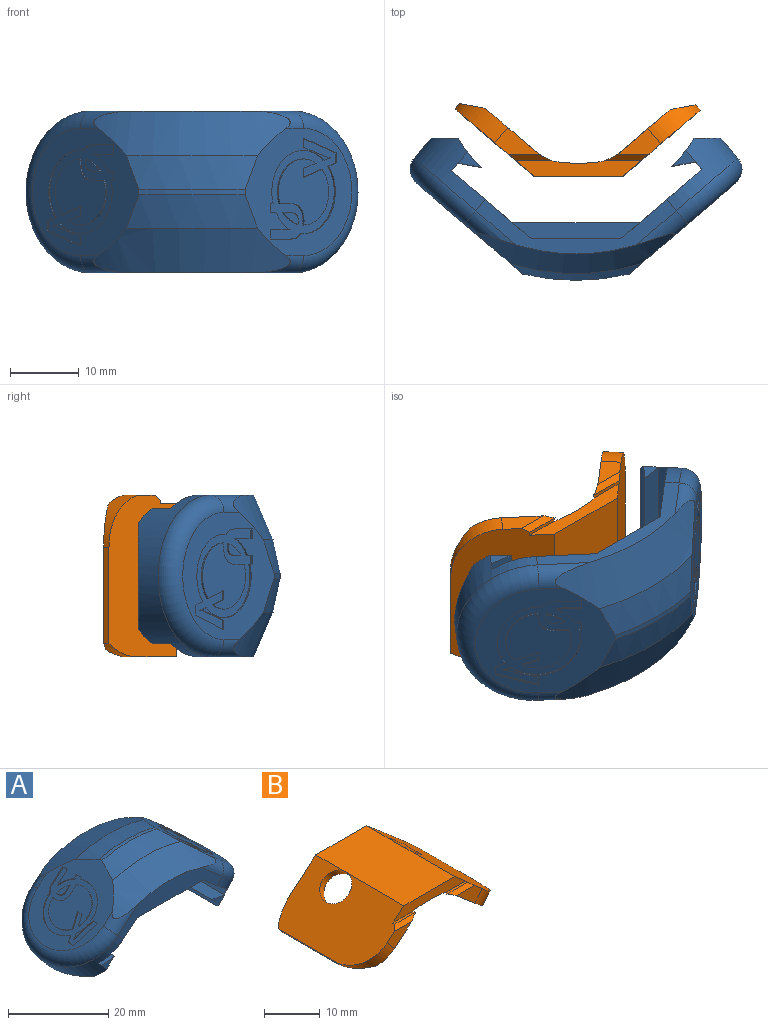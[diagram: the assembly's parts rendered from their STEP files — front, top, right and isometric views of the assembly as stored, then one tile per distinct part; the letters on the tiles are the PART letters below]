
ASSEMBLY  parts=2 mates=1
PART A: 220 faces, bbox 50.7x26.5x24.2 mm
  f0: plane 19.05x16.08mm, normal (0.65,0,0.76), area 158.9mm2, adj f27,f34,f35,f36,f37,f38,f39,f40
  f1: plane 19.05x16.08mm, normal (-0.65,0,0.76), area 158.9mm2, adj f27,f34,f35,f36,f37,f41,f42,f43
  f2: plane 20.57x16.8mm, normal (0.65,0,-0.76), area 311.5mm2, adj f10,f12,f46,f47,f108,f109,f110,f111
  f3: plane 20.57x17.09mm, normal (-0.65,0,-0.76), area 297.6mm2, adj f15,f44,f48,f49,f54,f55,f56,f57
  f4: plane 19.74x3.47mm, normal (-0.18,0,0.98), area 69.7mm2, adj f5,f21,f52,f53
  f5: cylinder r=20.13mm len=19.74mm, axis (0,-1,0), area 103.7mm2, adj f4,f6,f29,f52,f53
  f6: cylinder r=11.81mm len=23.62mm, axis (-0.65,0,0.76), area 146.7mm2, adj f5,f19,f21,f22,f29,f30,f31,f42
  f7: plane 19.38x3.49mm, normal (0.18,0,0.98), area 68.9mm2, adj f8,f23,f50,f51
  f8: cylinder r=20.13mm len=19.38mm, axis (0,-1,0), area 97.8mm2, adj f7,f9,f28,f50,f51
  f9: cylinder r=11.81mm len=23.62mm, axis (0.65,0,0.76), area 144.3mm2, adj f8,f23,f24,f25,f28,f30,f31,f39
  f10: cylinder r=1.52mm len=2.01mm, axis (-0.65,0,0.76), area 2mm2, adj f2,f11,f46,f47
  f11: torus R=12.7mm, axis (0,1,0), area 96.1mm2, adj f10,f44,f45,f46,f47,f48
  f12: cylinder r=10.29mm len=20.57mm, axis (0.65,0,-0.76), area 176.6mm2, adj f2,f19,f20,f21,f46,f47,f219
  f13: bspline ~11.23x4.8mm, area 4.8mm2, adj f18,f22,f47
  f14: bspline ~15.91x9.98mm, area 4.8mm2, adj f18,f19,f46
  f15: cylinder r=10.29mm len=20.57mm, axis (-0.65,0,-0.76), area 153.8mm2, adj f3,f23,f26,f48,f49,f215,f217
  f16: bspline ~5.86x4.5mm, area 8.5mm2, adj f18,f48,f215,f216
  f17: bspline ~15.92x9.99mm, area 8.5mm2, adj f18,f49,f217,f218
  f18: plane 23.12x13.75mm, normal (0,0,-1), area 226.4mm2, adj f13,f14,f16,f17,f19,f22,f24,f25
  f19: plane 13.42x11.6mm, normal (0.65,0,-0.76), area 33.8mm2, adj f6,f12,f14,f18,f21,f30,f32,f33
  f20: plane 15.97x2.89mm, normal (-0.65,0,0.76), area 42.2mm2, adj f12,f21
  f21: plane 19.8x1.94mm, normal (0.76,0,0.65), area 25.1mm2, adj f4,f6,f12,f19,f20,f22,f219
  f22: plane 13.42x11.61mm, normal (0.65,0,-0.76), area 16.6mm2, adj f6,f13,f18,f21,f31,f47,f219
  f23: plane 19.38x1.88mm, normal (-0.76,0,0.65), area 25.6mm2, adj f7,f9,f15,f24,f25,f26,f215,f217
  f24: plane 11.85x10.12mm, normal (-0.65,0,-0.76), area 10.9mm2, adj f9,f18,f23,f30,f32,f33,f215
  f25: plane 11.85x10.12mm, normal (-0.65,0,-0.76), area 15.1mm2, adj f9,f18,f23,f31,f217
  f26: plane 15.51x2.68mm, normal (0.65,0,0.76), area 38mm2, adj f15,f23
  f27: cylinder r=33.02mm len=15.5mm, axis (0,-1,0), area 11.9mm2, adj f0,f1,f36,f37
  f28: plane 15.7x3.93mm, normal (0,0,-1), area 42.3mm2, adj f8,f9
  f29: plane 15.7x3.93mm, normal (0,0,-1), area 42.3mm2, adj f5,f6
  f30: plane 29.25x7.95mm, normal (0,-1,0), area 102.8mm2, adj f6,f9,f19,f24,f32,f34,f40,f41
  f31: plane 29.25x7.95mm, normal (0,1,0), area 64.4mm2, adj f6,f9,f18,f22,f25,f35,f38,f43
  f32: plane 18.72x1.14mm, normal (0,0,-1), area 21.4mm2, adj f19,f24,f30,f33
  f33: plane 18.72x2.42mm, normal (0,1,0), area 38.4mm2, adj f18,f19,f24,f32
  f34: cone r=29.21mm half-angle=23.2deg, axis (0,1,0), area 181.7mm2, adj f0,f1,f30,f36,f40,f41
  f35: cone r=33.02mm half-angle=23.2deg, axis (0,-1,0), area 181.7mm2, adj f0,f1,f31,f37,f38,f43
  f36: cone r=33.02mm half-angle=11.6deg, axis (0,1,0), area 87.2mm2, adj f0,f1,f27,f34
  f37: cone r=33.02mm half-angle=11.6deg, axis (0,-1,0), area 87.2mm2, adj f0,f1,f27,f35
  f38: cylinder r=2.54mm len=7.47mm, axis (-0.76,0,0.65), area 16.1mm2, adj f0,f31,f35,f39
  f39: torus R=9.27mm, axis (0.65,0,0.76), area 136.5mm2, adj f0,f9,f38,f40
  f40: cylinder r=2.54mm len=7.47mm, axis (-0.76,0,0.65), area 16.1mm2, adj f0,f30,f34,f39
  f41: cylinder r=2.54mm len=7.47mm, axis (-0.76,0,-0.65), area 16.1mm2, adj f1,f30,f34,f42
  f42: torus R=9.27mm, axis (-0.65,0,0.76), area 136.5mm2, adj f1,f6,f41,f43
  f43: cylinder r=2.54mm len=7.47mm, axis (-0.76,0,-0.65), area 16.1mm2, adj f1,f31,f35,f42
  f44: cylinder r=1.91mm len=5.15mm, axis (0.65,0,0.76), area 11.8mm2, adj f3,f11,f18,f48,f49
  f45: cylinder r=1.52mm len=2.44mm, axis (-0.65,0,0.76), area 6mm2, adj f11,f18,f46,f47
  f46: cylinder r=12.7mm len=5.61mm, axis (0.65,0,-0.76), area 15mm2, adj f2,f10,f11,f12,f14,f18,f19,f45
  f47: cylinder r=12.7mm len=6.97mm, axis (-0.65,0,0.76), area 17.7mm2, adj f2,f10,f11,f12,f13,f18,f22,f45
  f48: cylinder r=12.7mm len=6mm, axis (0.65,0,0.76), area 16.9mm2, adj f3,f11,f15,f16,f18,f44,f216
  f49: cylinder r=12.7mm len=6mm, axis (-0.65,0,-0.76), area 17.1mm2, adj f3,f15,f17,f18,f44,f218
  f50: plane 3.49x2.32mm, normal (0,1,0), area 3.3mm2, adj f7,f8,f9
  f51: plane 3.49x2.32mm, normal (0,-1,0), area 3.3mm2, adj f7,f8,f9
  f52: plane 3.47x2.27mm, normal (0,1,0), area 3.1mm2, adj f4,f5,f6
  f53: plane 3.47x2.27mm, normal (0,-1,0), area 3.1mm2, adj f4,f5,f6
  f54: plane 1.1x0.99mm, normal (0,1,0), area 0.3mm2, adj f3,f55,f61,f62
  f55: plane 0.8x0.19mm, normal (0.76,0,-0.65), area 0.2mm2, adj f3,f54,f56,f62
  f56: plane 2.77x2.42mm, normal (0,-1,0), area 0.9mm2, adj f3,f55,f57,f62
  f57: plane 0.8x0.19mm, normal (-0.76,0,0.65), area 0.2mm2, adj f3,f56,f58,f62
  f58: plane 1.1x0.99mm, normal (0,1,0), area 0.3mm2, adj f3,f57,f59,f62
  f59: plane 3.73x0.19mm, normal (-0.76,0,0.65), area 0.9mm2, adj f3,f58,f60,f62
  f60: plane 0.9x0.82mm, normal (0,1,0), area 0.2mm2, adj f3,f59,f61,f62
  f61: plane 3.73x0.19mm, normal (0.76,0,-0.65), area 0.9mm2, adj f3,f54,f60,f62
  f62: plane 4.53x2.6mm, normal (-0.65,0,-0.76), area 6.3mm2, adj f54,f55,f56,f57,f58,f59,f60,f61
  f63: plane 2.93x0.19mm, normal (0.76,0,-0.65), area 0.7mm2, adj f3,f64,f77,f78
  f64: plane 0.89x0.82mm, normal (0,-1,0), area 0.2mm2, adj f3,f63,f65,f78
  f65: plane 2.77x0.19mm, normal (-0.76,0,0.65), area 0.7mm2, adj f3,f64,f66,f78
  f66: extruded ~0.77x0.33mm, area 0.2mm2, adj f3,f65,f67,f78
  f67: extruded ~0.68x0.64mm, area 0.2mm2, adj f3,f66,f68,f78
  f68: extruded ~0.7x0.65mm, area 0.2mm2, adj f3,f67,f69,f78
  f69: extruded ~0.77x0.33mm, area 0.2mm2, adj f3,f68,f70,f78
  f70: plane 2.78x0.19mm, normal (0.76,0,-0.65), area 0.7mm2, adj f3,f69,f71,f78
  f71: plane 0.89x0.82mm, normal (0,-1,0), area 0.2mm2, adj f3,f70,f72,f78
  f72: plane 2.92x0.19mm, normal (-0.76,0,0.65), area 0.7mm2, adj f3,f71,f73,f78
  f73: extruded ~1.23x0.53mm, area 0.3mm2, adj f3,f72,f74,f78
  f74: extruded ~1.2x1.08mm, area 0.4mm2, adj f3,f73,f75,f78
  f75: extruded ~0.93x0.85mm, area 0.3mm2, adj f3,f74,f76,f78
  f76: extruded ~0.66x0.62mm, area 0.2mm2, adj f3,f75,f77,f78
  f77: extruded ~0.88x0.34mm, area 0.2mm2, adj f3,f63,f76,f78
  f78: plane 4.6x2.83mm, normal (-0.65,0,-0.76), area 9.4mm2, adj f63,f64,f65,f66,f67,f68,f69,f70
  f79: plane 1.69x1.49mm, normal (0,1,0), area 0.5mm2, adj f3,f80,f90,f91
  f80: plane 1.99x0.19mm, normal (-0.76,0,0.65), area 0.5mm2, adj f3,f79,f81,f91
  f81: plane 1.03x0.93mm, normal (0,1,0), area 0.3mm2, adj f3,f80,f82,f91
  f82: plane 1.99x0.19mm, normal (0.76,0,-0.65), area 0.5mm2, adj f3,f81,f83,f91
  f83: plane 1.69x1.49mm, normal (0,1,0), area 0.5mm2, adj f3,f82,f84,f91
  f84: plane 1.13x0.19mm, normal (0.76,0,-0.65), area 0.3mm2, adj f3,f83,f85,f91
  f85: plane 1.69x1.49mm, normal (0,-1,0), area 0.5mm2, adj f3,f84,f86,f91
  f86: plane 2.02x0.19mm, normal (0.76,0,-0.65), area 0.5mm2, adj f3,f85,f87,f91
  f87: plane 1.03x0.93mm, normal (0,-1,0), area 0.3mm2, adj f3,f86,f88,f91
  f88: plane 2.02x0.19mm, normal (-0.76,0,0.65), area 0.5mm2, adj f3,f87,f89,f91
  f89: plane 1.69x1.49mm, normal (0,-1,0), area 0.5mm2, adj f3,f88,f90,f91
  f90: plane 1.13x0.19mm, normal (-0.76,0,0.65), area 0.3mm2, adj f3,f79,f89,f91
  f91: plane 5.14x3.9mm, normal (-0.65,0,-0.76), area 10.3mm2, adj f79,f80,f81,f82,f83,f84,f85,f86
  f92: extruded ~1.14x0.38mm, area 0.3mm2, adj f93,f105,f106,f107
  f93: extruded ~1.15x0.39mm, area 0.3mm2, adj f92,f94,f106,f107
  f94: extruded ~0.82x0.76mm, area 0.3mm2, adj f93,f95,f106,f107
  f95: extruded ~1.53x1.03mm, area 0.6mm2, adj f94,f96,f106,f107
  f96: extruded ~1.53x1.04mm, area 0.6mm2, adj f95,f105,f106,f107
  f97: extruded ~1.73x0.59mm, area 0.5mm2, adj f3,f98,f104,f106
  f98: extruded ~1.73x0.59mm, area 0.5mm2, adj f3,f97,f99,f106
  f99: extruded ~1.38x1.23mm, area 0.4mm2, adj f3,f98,f100,f106
  f100: extruded ~1.38x1.24mm, area 0.4mm2, adj f3,f99,f101,f106
  f101: extruded ~1.73x0.59mm, area 0.5mm2, adj f3,f100,f102,f106
  f102: extruded ~1.74x0.59mm, area 0.5mm2, adj f3,f101,f103,f106
  f103: extruded ~1.38x1.23mm, area 0.4mm2, adj f3,f102,f104,f106
  f104: extruded ~1.38x1.23mm, area 0.4mm2, adj f3,f97,f103,f106
  f105: extruded ~0.82x0.75mm, area 0.2mm2, adj f92,f96,f106,f107
  f106: plane 4.67x3.28mm, normal (-0.65,0,-0.76), area 10.8mm2, adj f92,f93,f94,f95,f96,f97,f98,f99
  f107: plane 3.06x1.75mm, normal (-0.65,0,-0.76), area 5.9mm2, adj f92,f93,f94,f95,f96,f105
  f108: plane 1.09x0.99mm, normal (0,1,0), area 0.3mm2, adj f2,f109,f121,f122
  f109: plane 4.53x0.19mm, normal (0.76,0,0.65), area 1.2mm2, adj f2,f108,f110,f122
  f110: plane 0.82x0.76mm, normal (0,-1,0), area 0.2mm2, adj f2,f109,f111,f122
  f111: plane 2.15x0.19mm, normal (-0.76,0,-0.65), area 0.5mm2, adj f2,f110,f112,f122
  f112: extruded ~1.25x0.22mm, area 0.3mm2, adj f2,f111,f113,f122
  f113: plane 0.21x0.18mm, normal (0,-1,0), area 0mm2, adj f2,f112,f114,f122
  f114: plane 3.4x1.66mm, normal (0.66,-0.5,0.56), area 1mm2, adj f2,f113,f115,f122
  f115: plane 1.09x0.98mm, normal (0,-1,0), area 0.3mm2, adj f2,f114,f116,f122
  f116: plane 4.53x0.19mm, normal (-0.76,0,-0.65), area 1.2mm2, adj f2,f115,f117,f122
  f117: plane 0.82x0.75mm, normal (0,1,0), area 0.2mm2, adj f2,f116,f118,f122
  f118: plane 2.13x0.19mm, normal (0.76,0,0.65), area 0.5mm2, adj f2,f117,f119,f122
  f119: extruded ~1.3x0.23mm, area 0.3mm2, adj f2,f118,f120,f122
  f120: plane 0.21x0.19mm, normal (0,1,0), area 0mm2, adj f2,f119,f121,f122
  f121: plane 3.43x1.66mm, normal (-0.66,0.5,-0.56), area 1mm2, adj f2,f108,f120,f122
  f122: plane 4.53x3.06mm, normal (0.65,0,-0.76), area 11.6mm2, adj f108,f109,f110,f111,f112,f113,f114,f115
  f123: plane 4.53x0.19mm, normal (-0.76,0,-0.65), area 1.2mm2, adj f2,f124,f126,f127
  f124: plane 0.9x0.82mm, normal (0,1,0), area 0.2mm2, adj f2,f123,f125,f127
  f125: plane 4.53x0.19mm, normal (0.76,0,0.65), area 1.2mm2, adj f2,f124,f126,f127
  f126: plane 0.9x0.82mm, normal (0,-1,0), area 0.2mm2, adj f2,f123,f125,f127
  f127: plane 4.53x0.73mm, normal (0.65,0,-0.76), area 4.4mm2, adj f123,f124,f125,f126
  f128: plane 1.69x1.49mm, normal (0,1,0), area 0.5mm2, adj f2,f129,f139,f140
  f129: plane 1.99x0.19mm, normal (-0.76,0,-0.65), area 0.5mm2, adj f2,f128,f130,f140
  f130: plane 1.03x0.93mm, normal (0,1,0), area 0.3mm2, adj f2,f129,f131,f140
  f131: plane 1.99x0.19mm, normal (0.76,0,0.65), area 0.5mm2, adj f2,f130,f132,f140
  f132: plane 1.69x1.49mm, normal (0,1,0), area 0.5mm2, adj f2,f131,f133,f140
  f133: plane 1.13x0.19mm, normal (0.76,0,0.65), area 0.3mm2, adj f2,f132,f134,f140
  f134: plane 1.69x1.49mm, normal (0,-1,0), area 0.5mm2, adj f2,f133,f135,f140
  f135: plane 2.02x0.19mm, normal (0.76,0,0.65), area 0.5mm2, adj f2,f134,f136,f140
  f136: plane 1.03x0.93mm, normal (0,-1,0), area 0.3mm2, adj f2,f135,f137,f140
  f137: plane 2.02x0.19mm, normal (-0.76,0,-0.65), area 0.5mm2, adj f2,f136,f138,f140
  f138: plane 1.69x1.49mm, normal (0,-1,0), area 0.5mm2, adj f2,f137,f139,f140
  f139: plane 1.13x0.19mm, normal (-0.76,0,-0.65), area 0.3mm2, adj f2,f128,f138,f140
  f140: plane 5.14x3.9mm, normal (0.65,0,-0.76), area 10.3mm2, adj f128,f129,f130,f131,f132,f133,f134,f135
  f141: plane 1.91x1.69mm, normal (0,1,0), area 0.6mm2, adj f142,f174,f175,f177
  f142: cylinder r=4.83mm len=6.51mm, axis (-0.65,0,0.76), area 3mm2, adj f141,f143,f175,f177
  f143: plane 1.95x1.72mm, normal (-0.23,0.95,-0.2), area 0.6mm2, adj f142,f144,f175,f177
  f144: plane 1.35x0.19mm, normal (-0.76,0,-0.65), area 0.3mm2, adj f143,f145,f175,f177
  f145: plane 2.81x2.46mm, normal (0.24,-0.95,0.21), area 0.9mm2, adj f144,f146,f175,f177
  f146: cylinder r=4.83mm len=8.11mm, axis (-0.65,0,0.76), area 2.8mm2, adj f145,f147,f175,f177
  f147: extruded ~0.53x0.21mm, area 0.1mm2, adj f146,f148,f175,f177
  f148: extruded ~1.4x0.38mm, area 0.4mm2, adj f147,f149,f175,f177
  f149: extruded ~0.9x0.78mm, area 0.3mm2, adj f148,f174,f175,f177
  f150: cylinder r=4.83mm len=2.21mm, axis (-0.65,0,0.76), area 0.8mm2, adj f151,f172,f175,f176
  f151: plane 1.16x1.05mm, normal (0,-1,0), area 0.3mm2, adj f150,f152,f175,f176
  f152: extruded ~0.98x0.89mm, area 0.3mm2, adj f151,f153,f175,f176
  f153: extruded ~0.95x0.43mm, area 0.3mm2, adj f152,f172,f175,f176
  f154: plane 0.5x0.48mm, normal (0,1,0), area 0.1mm2, adj f1,f155,f173,f175
  f155: plane 1.33x0.19mm, normal (-0.76,0,-0.65), area 0.3mm2, adj f1,f154,f156,f175
  f156: plane 0.93x0.84mm, normal (0,-1,0), area 0.3mm2, adj f1,f155,f157,f175
  f157: cylinder r=6.1mm len=2.51mm, axis (-0.65,0,0.76), area 1mm2, adj f1,f156,f158,f175
  f158: plane 3x2.61mm, normal (0,1,0), area 0.9mm2, adj f1,f157,f159,f175
  f159: plane 1.33x0.19mm, normal (-0.76,0,-0.65), area 0.3mm2, adj f1,f158,f160,f175
  f160: plane 3.25x2.83mm, normal (0,-1,0), area 1mm2, adj f1,f159,f161,f175
  f161: extruded ~1.46x1.3mm, area 0.5mm2, adj f1,f160,f162,f175
  f162: extruded ~0.25x0.23mm, area 0mm2, adj f1,f161,f163,f175
  f163: cylinder r=6.1mm len=9.82mm, axis (-0.65,0,0.76), area 3.6mm2, adj f1,f162,f164,f175
  f164: plane 1.32x1.18mm, normal (0.24,-0.95,0.21), area 0.4mm2, adj f1,f163,f165,f175
  f165: plane 1.46x0.19mm, normal (0.76,0,0.65), area 0.4mm2, adj f1,f164,f166,f175
  f166: plane 4.95x4.28mm, normal (0.24,0.95,0.21), area 1.7mm2, adj f1,f165,f167,f175
  f167: plane 1.35x0.19mm, normal (-0.76,0,-0.65), area 0.3mm2, adj f1,f166,f168,f175
  f168: plane 3.01x2.63mm, normal (-0.23,-0.95,-0.2), area 1mm2, adj f1,f167,f169,f175
  f169: extruded ~1.22x1.09mm, area 0.4mm2, adj f1,f168,f170,f175
  f170: extruded ~0.63x0.59mm, area 0.2mm2, adj f1,f169,f171,f175
  f171: extruded ~0.66x0.62mm, area 0.2mm2, adj f1,f170,f173,f175
  f172: extruded ~0.44x0.22mm, area 0.1mm2, adj f150,f153,f175,f176
  f173: cylinder r=6.1mm len=7.78mm, axis (-0.65,0,0.76), area 3.9mm2, adj f1,f154,f171,f175
  f174: extruded ~1.1x0.99mm, area 0.3mm2, adj f141,f149,f175,f177
  f175: plane 14.69x9.61mm, normal (-0.65,0,0.76), area 71.5mm2, adj f141,f142,f143,f144,f145,f146,f147,f148
  f176: plane 2.08x1.77mm, normal (-0.65,0,0.76), area 2.6mm2, adj f150,f151,f152,f153,f172
  f177: plane 9.65x7.34mm, normal (-0.65,0,0.76), area 59.8mm2, adj f141,f142,f143,f144,f145,f146,f147,f148
  f178: cylinder r=4.83mm len=2.21mm, axis (0.65,0,0.76), area 0.8mm2, adj f179,f211,f212,f214
  f179: plane 1.16x1.05mm, normal (0,1,0), area 0.3mm2, adj f178,f180,f212,f214
  f180: extruded ~0.98x0.89mm, area 0.3mm2, adj f179,f181,f212,f214
  f181: extruded ~0.95x0.43mm, area 0.3mm2, adj f180,f211,f212,f214
  f182: plane 2.81x2.46mm, normal (-0.24,0.95,0.21), area 0.9mm2, adj f183,f209,f212,f213
  f183: cylinder r=4.83mm len=8.11mm, axis (0.65,0,0.76), area 2.8mm2, adj f182,f184,f212,f213
  f184: extruded ~0.53x0.21mm, area 0.1mm2, adj f183,f185,f212,f213
  f185: extruded ~1.4x0.38mm, area 0.4mm2, adj f184,f186,f212,f213
  f186: extruded ~0.9x0.78mm, area 0.3mm2, adj f185,f187,f212,f213
  f187: extruded ~1.1x0.99mm, area 0.3mm2, adj f186,f188,f212,f213
  f188: plane 1.91x1.69mm, normal (0,-1,0), area 0.6mm2, adj f187,f189,f212,f213
  f189: cylinder r=4.83mm len=6.51mm, axis (0.65,0,0.76), area 3mm2, adj f188,f190,f212,f213
  f190: plane 1.95x1.72mm, normal (0.23,-0.95,-0.2), area 0.6mm2, adj f189,f209,f212,f213
  f191: extruded ~0.66x0.62mm, area 0.2mm2, adj f0,f192,f210,f212
  f192: cylinder r=6.1mm len=7.78mm, axis (0.65,0,0.76), area 3.9mm2, adj f0,f191,f193,f212
  f193: plane 0.5x0.48mm, normal (0,-1,0), area 0.1mm2, adj f0,f192,f194,f212
  f194: plane 1.33x0.19mm, normal (0.76,0,-0.65), area 0.3mm2, adj f0,f193,f195,f212
  f195: plane 0.93x0.84mm, normal (0,1,0), area 0.3mm2, adj f0,f194,f196,f212
  f196: cylinder r=6.1mm len=2.51mm, axis (0.65,0,0.76), area 1mm2, adj f0,f195,f197,f212
  f197: plane 3x2.61mm, normal (0,-1,0), area 0.9mm2, adj f0,f196,f198,f212
  f198: plane 1.33x0.19mm, normal (0.76,0,-0.65), area 0.3mm2, adj f0,f197,f199,f212
  f199: plane 3.25x2.83mm, normal (0,1,0), area 1mm2, adj f0,f198,f200,f212
  f200: extruded ~1.46x1.3mm, area 0.5mm2, adj f0,f199,f201,f212
  f201: extruded ~0.25x0.23mm, area 0mm2, adj f0,f200,f202,f212
  f202: cylinder r=6.1mm len=9.82mm, axis (0.65,0,0.76), area 3.6mm2, adj f0,f201,f203,f212
  f203: plane 1.32x1.18mm, normal (-0.24,0.95,0.21), area 0.4mm2, adj f0,f202,f204,f212
  f204: plane 1.46x0.19mm, normal (-0.76,0,0.65), area 0.4mm2, adj f0,f203,f205,f212
  f205: plane 4.95x4.28mm, normal (-0.24,-0.95,0.21), area 1.7mm2, adj f0,f204,f206,f212
  f206: plane 1.35x0.19mm, normal (0.76,0,-0.65), area 0.3mm2, adj f0,f205,f207,f212
  f207: plane 3.01x2.63mm, normal (0.23,0.95,-0.2), area 1mm2, adj f0,f206,f208,f212
  f208: extruded ~1.22x1.09mm, area 0.4mm2, adj f0,f207,f210,f212
  f209: plane 1.35x0.19mm, normal (0.76,0,-0.65), area 0.3mm2, adj f182,f190,f212,f213
  f210: extruded ~0.63x0.59mm, area 0.2mm2, adj f0,f191,f208,f212
  f211: extruded ~0.44x0.22mm, area 0.1mm2, adj f178,f181,f212,f214
  f212: plane 14.69x9.61mm, normal (0.65,0,0.76), area 71.5mm2, adj f178,f179,f180,f181,f182,f183,f184,f185
  f213: plane 9.65x7.34mm, normal (0.65,0,0.76), area 59.8mm2, adj f182,f183,f184,f185,f186,f187,f188,f189
  f214: plane 2.08x1.77mm, normal (0.65,0,0.76), area 2.6mm2, adj f178,f179,f180,f181,f211
  f215: cone r=10.29mm half-angle=51.3deg, axis (-0.65,0,-0.76), area 28.6mm2, adj f15,f16,f18,f23,f24,f216
  f216: cone r=11.43mm half-angle=51.3deg, axis (0.65,0,0.76), area 0mm2, adj f16,f48,f215
  f217: cone r=10.29mm half-angle=51.3deg, axis (-0.65,0,-0.76), area 28.6mm2, adj f15,f17,f18,f23,f25,f218
  f218: cone r=11.43mm half-angle=51.3deg, axis (0.65,0,0.76), area 0mm2, adj f17,f49,f217
  f219: cone r=10.29mm half-angle=51.3deg, axis (0.65,0,-0.76), area 28.7mm2, adj f12,f21,f22,f47
PART B: 62 faces, bbox 35.9x28.6x12.3 mm
  f0: plane 6.48x3.83mm, normal (0,-1,0), area 12.2mm2, adj f8,f13,f15,f47,f52
  f1: plane 6.68x4mm, normal (0,-1,0), area 13mm2, adj f7,f12,f14,f46,f51
  f2: cone r=20.13mm half-angle=9.1deg, axis (0,1,0), area 10.4mm2, adj f12,f13,f17,f50
  f3: plane 22.49x12.99mm, normal (0,0,1), area 287.2mm2, adj f7,f8,f9,f10,f11,f50
  f4: cylinder r=11.81mm len=5.98mm, axis (-0.65,0,0.76), area 11.7mm2, adj f8,f9,f28,f29,f60,f61
  f5: cylinder r=11.81mm len=6.19mm, axis (0.65,0,0.76), area 12.3mm2, adj f7,f9,f26,f27,f53,f54
  f6: cylinder r=20.13mm len=19.79mm, axis (0,-1,0), area 12.4mm2, adj f14,f26,f46,f53
  f7: plane 23.62x11.56mm, normal (0.65,0,0.76), area 304.1mm2, adj f1,f3,f5,f9,f10,f27,f46,f48
  f8: plane 23.62x11.35mm, normal (-0.65,0,0.76), area 298.2mm2, adj f0,f3,f4,f9,f11,f28,f47,f49
  f9: plane 26.12x7.12mm, normal (0,1,0), area 44.2mm2, adj f3,f4,f5,f7,f8,f55,f56,f57
  f10: cylinder r=3.26mm len=6.53mm, axis (-0.65,0,-0.76), area 35.6mm2, adj f3,f7,f40,f41,f42,f43,f44,f45
  f11: cylinder r=3.26mm len=6.53mm, axis (0.65,0,-0.76), area 35.6mm2, adj f3,f8,f34,f35,f36,f37,f38,f39
  f12: bspline ~9.89x4.98mm, area 6.3mm2, adj f1,f2,f14,f17,f19,f30,f48,f50
  f13: bspline ~12.9x5.76mm, area 6.3mm2, adj f0,f2,f15,f17,f21,f32,f49,f50
  f14: plane 21.08x7.64mm, normal (-0.65,0,-0.76), area 128.4mm2, adj f1,f6,f12,f19,f23,f30,f43,f46
  f15: plane 21.08x7.64mm, normal (0.65,0,-0.76), area 128.2mm2, adj f0,f13,f16,f21,f25,f32,f37,f47
  f16: cylinder r=20.13mm len=19.64mm, axis (0,-1,0), area 7.4mm2, adj f15,f29,f47,f61
  f17: cylinder r=23.18mm len=18.03mm, axis (0,-1,0), area 103.8mm2, adj f2,f12,f13,f18,f19,f20,f21,f22
  f18: bspline ~3.55x3.04mm, area 1.6mm2, adj f17,f19,f40
  f19: cylinder r=5.08mm len=10.28mm, axis (0,-1,0), area 25.3mm2, adj f12,f14,f17,f18,f30,f41
  f20: bspline ~3.55x3.04mm, area 1.6mm2, adj f17,f21,f38
  f21: cylinder r=5.08mm len=10.28mm, axis (0,-1,0), area 25.3mm2, adj f13,f15,f17,f20,f32,f39
  f22: bspline ~3.55x3.04mm, area 1.6mm2, adj f17,f23,f44
  f23: cylinder r=5.08mm len=2.7mm, axis (0,-1,0), area 5.6mm2, adj f14,f17,f22,f45,f56
  f24: bspline ~3.55x3.04mm, area 1.6mm2, adj f17,f25,f34
  f25: cylinder r=5.08mm len=2.7mm, axis (0,-1,0), area 5.6mm2, adj f15,f17,f24,f35,f58
  f26: plane 21.35x3.87mm, normal (-0.18,0,-0.98), area 71.4mm2, adj f5,f6,f27,f46,f53
  f27: plane 14.07x0.77mm, normal (0.76,0,-0.65), area 14.3mm2, adj f5,f7,f26,f46
  f28: plane 14.24x0.77mm, normal (-0.76,0,-0.65), area 14.5mm2, adj f4,f8,f29,f47
  f29: plane 21.46x3.87mm, normal (0.18,0,-0.98), area 71.6mm2, adj f4,f16,f28,f47,f61
  f30: cylinder r=3.43mm len=6.86mm, axis (-0.65,0,-0.76), area 2.3mm2, adj f12,f14,f19,f31
  f31: plane 6.86x5.21mm, normal (-0.65,0,-0.76), area 36.9mm2, adj f30
  f32: cylinder r=3.43mm len=6.86mm, axis (0.65,0,-0.76), area 4.1mm2, adj f13,f15,f21,f33
  f33: plane 6.86x5.21mm, normal (0.65,0,-0.76), area 36.9mm2, adj f32
  f34: bspline ~2.54x1.85mm, area 3.1mm2, adj f11,f24,f35,f36
  f35: bspline ~2.31x2.06mm, area 2.8mm2, adj f11,f25,f34,f37
  f36: bspline ~1.19x0.69mm, area 0.7mm2, adj f11,f17,f34,f38
  f37: cone r=4.53mm half-angle=45deg, axis (0.65,0,-0.76), area 28.4mm2, adj f11,f15,f35,f39
  f38: bspline ~2.54x1.85mm, area 3.1mm2, adj f11,f20,f36,f39
  f39: bspline ~2.31x2.06mm, area 2.8mm2, adj f11,f21,f37,f38
  f40: bspline ~2.54x1.85mm, area 3.1mm2, adj f10,f18,f41,f42
  f41: bspline ~2.31x2.06mm, area 2.8mm2, adj f10,f19,f40,f43
  f42: bspline ~1.19x0.69mm, area 0.7mm2, adj f10,f17,f40,f44
  f43: cone r=4.53mm half-angle=45deg, axis (-0.65,0,-0.76), area 28.4mm2, adj f10,f14,f41,f45
  f44: bspline ~2.54x1.85mm, area 3.1mm2, adj f10,f22,f42,f45
  f45: bspline ~2.31x2.06mm, area 2.8mm2, adj f10,f23,f43,f44
  f46: cylinder r=7.62mm len=7.7mm, axis (-0.65,0,-0.76), area 25.8mm2, adj f1,f6,f7,f14,f26,f27
  f47: cylinder r=7.62mm len=7.69mm, axis (-0.65,0,0.76), area 25.7mm2, adj f0,f8,f15,f16,f28,f29
  f48: plane 5.31x0.53mm, normal (0,0,1), area 2.6mm2, adj f7,f12,f50,f51
  f49: plane 5.31x0.53mm, normal (0,0,1), area 2.6mm2, adj f8,f13,f50,f52
  f50: plane 18.46x2.4mm, normal (0,-1,0), area 34.8mm2, adj f2,f3,f7,f8,f12,f13,f48,f49
  f51: plane 6.28x0.86mm, normal (0,-0.71,0.71), area 5.2mm2, adj f1,f7,f12,f48
  f52: plane 6.28x0.86mm, normal (0,-0.71,0.71), area 5.2mm2, adj f0,f8,f13,f49
  f53: bspline ~2.92x2.42mm, area 3.3mm2, adj f5,f6,f26,f54
  f54: cone r=9.27mm half-angle=68.2deg, axis (0.65,0,0.76), area 7.9mm2, adj f5,f14,f53,f55
  f55: plane 6.38x5.66mm, normal (-0.6,0.37,-0.71), area 20.6mm2, adj f9,f14,f54,f56
  f56: cone r=6.1mm half-angle=21.8deg, axis (0,1,0), area 9mm2, adj f9,f23,f55,f57
  f57: cone r=23.18mm half-angle=21.8deg, axis (0,1,0), area 15.3mm2, adj f9,f17,f56,f58
  f58: cone r=6.1mm half-angle=21.8deg, axis (0,1,0), area 9mm2, adj f9,f25,f57,f59
  f59: plane 6.38x5.66mm, normal (0.6,0.37,-0.71), area 20.6mm2, adj f9,f15,f58,f60
  f60: cone r=11.81mm half-angle=68.2deg, axis (-0.65,0,0.76), area 7.9mm2, adj f4,f15,f59,f61
  f61: bspline ~2.86x2.29mm, area 2.5mm2, adj f4,f16,f29,f60
PLACE A rot(axis=(1,0,0),90deg) t=(-2.17,37.84,9.07)mm
PLACE B rot(axis=(0,-0.71,0.71),180deg) t=(-1.81,46.66,64.7)mm
MATE planar A.f30 <-> B.f9  axis (0,0,-1) through (-2.17,13.71,25.08)mm
